# Revit family: 180
name_source: partatom
category: Plumbing Fixtures
units: mm (PartAtom-declared; Revit-internal decimal feet)

## family parameters
Always vertical = Yes
Cut with Voids When Loaded = No
Enable Cutting in Views = No
Maintain Annotation Orientation = No
OmniClass Number = 23.45.55.00
OmniClass Title = Sanitary Faucets, Wastes
Part Type = Normal
Room Calculation Point = No
Round Connector Dimension = Use Diameter
Shared = No
Work Plane-Based = No

## types (1)
- 180 Washing machine valve, G3/4xG1/2
    3D View = https://static.oras.com
    AssetType = Fixed
    BIMObjectName = 180
    Backflow Prevention EN1717 = HB
    BodyMaterial = Brass
    Brand = Oras
    CO2 Emissions (A1-A3) = 2.71
    CO2 Emissions (A4) = 0.13
    CO2 Emissions (C2) = 0.01
    CO2 Emissions (C3) = 0
    CO2 Emissions (C4) = 0
    CO2 Emissions (D) = -1.12
    Catalog Drawing URL = http://static.oras.com
    Category B2C = Bathroom
    CloseOffRating = 0
    Color = Chrome
    Connection = One inlet for cold or premixed water
    Connection Size = G3/4 x G1/2
    Default Elevation = 0 mm  [stored 0 ft]
    Dimension Drawing URL = http://static.oras.com
    DurationUnit = Year
    ETIM Class Number = EC011375 Water tap
    Export Type to IFC As = IfcValveType
    FDV Document URL = http://www.oras.com
    FaucetMainMaterial = Chrome
    Finish = Polished
    Flow Drawing URL = http://static.oras.com
    Flow Rate At 300kPa = 0.5 L/s
    FlowCoefficient = 0
    Group = Washing machine valve
    IfcExportAs = IfcValveType
    IfcExportType = FAUCET
    Installation Type = Wall mounted
    Interactive AR View URL = https://static.oras.com
    LVI Number = 6219530
    Lever Handle = Flow control handle
    Manufacturer = Oras
    ManufacturerName = Oras
    ManufacturerURL = http://www.oras.com
    Market = Estonia;Finland;International;Lithuania;Latvia;Poland
    Material = Brass
    Max. Hot Water Supply = 80 °C
    Mechanical Parts = Ceramic head part for flow control;Vacuum breaker
    Mobile Product Information URL = http://mpi.oras.com
    Model = 180 Washing machine valve, G3/4xG1/2
    ModelReference = 180
    NBSDescription = Water supply fittings for wash basins and troughs
    NBSReference = 45-35-70/371
    Name = 180 Washing machine valve, G3/4xG1/2
    Name_en = 180 Washing machine valve, G3/4xG1/2
    Noise Class = I (ISO 3822)
    NominalDepth = 90 mm
    NominalHeight = 80 mm
    NominalWidth = 34 mm  [stored 0.111549 ft]
    Pressure Loss With Flow 02ls = 55000.0 Pa
    Product Code = 180
    Product Family = Oras
    Product Image URL = http://static.oras.com
    Product URL = http://static.oras.com
    STF Certificate = EUFI29-22000144-TH6
    Shape = Sculptured
    ShowerDefaultElevation = 900 mm  [stored 2.95276 ft]
    Size = 35x90x80 mm
    Spare-Part Information URL = http://static.oras.com
    Surface treatment = Chrome
    Technical DataSheet URL = http://www.oras.com
    Type IFC Predefined Type = FAUCET
    UNSPSC Class Number = 30181800 Faucet and shower heads, jets and parts and accessories
    URL Declaration Of Performance (DOP) = http://static.oras.com
    URL Declaration of Asbestos = http://static.oras.com
    URL Declaration of Conformity = http://static.oras.com
    URL Declaration of SCIP = http://static.oras.com
    URL EU Packaging Declaration = http://static.oras.com
    URL EcoLabel Declaration = http://static.oras.com
    URL Environmental Product Declaration EPD = http://static.oras.com
    URL Materials Declaration = http://www.oras.com
    URL REACH = http://static.oras.com
    URL STF = http://static.oras.com
    Uniclass2 = Pr_40_30_96_96
    Uniclass2015Description = Washbasin manual water supply sets
    Uniclass2015Reference = Pr_40_20_87_96
    Version = 1
    VersionDate = 2025/10/01
    Warranty Information URL = http://warranty.oras.com
    WarrantyDescription = http://warranty.oras.com
    WarrantyDurationUnit = Year
    Working Pressure = 100 - 1000 kPa

note: [stored X ft] marks values corroborated as IEEE doubles in the binary element streams (Revit-internal decimal feet)

## geometry (parser evidence)
native form markers: Sweep x5
no freeform markers — native parametric forms only
